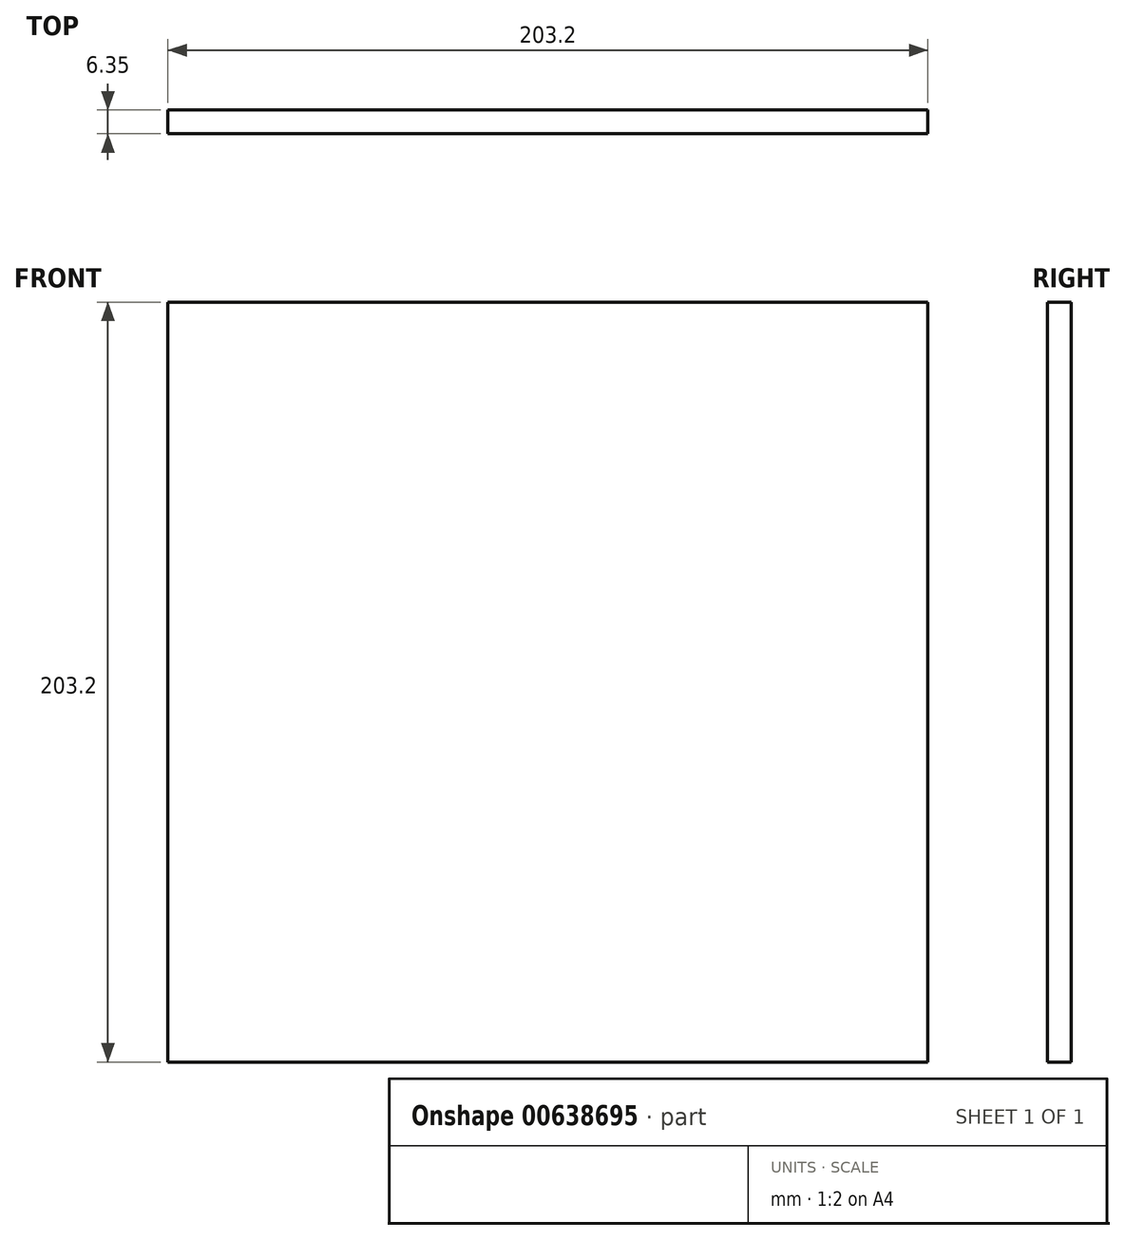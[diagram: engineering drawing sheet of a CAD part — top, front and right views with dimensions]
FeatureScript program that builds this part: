
annotation { "Feature Type Name" : "Feature", "Feature Type Description" : "" }
export const myFeature = defineFeature(function(context is Context, id is Id, definition is map)
    precondition{}
    {
        {
            var Q0;
            Q0=qCreatedBy(makeId("Front.planeOp"),FACE);
            var sketch = newSketch(context, id + "F0", { "sketchPlane" : qUnion([Q0])});
            skLineSegment(sketch, "E0.bottom", {"start": v(0, 0) * mm, "end": v(203.2, 0) * mm});
            skLineSegment(sketch, "E0.top", {"start": v(0, 203.2) * mm, "end": v(203.2, 203.2) * mm});
            skLineSegment(sketch, "E0.left", {"start": v(0, 0) * mm, "end": v(0, 203.2) * mm});
            skLineSegment(sketch, "E0.right", {"start": v(203.2, 0) * mm, "end": v(203.2, 203.2) * mm});
            skSolve(sketch);
        }
        {
            var Q0;
            Q0 = qSketchRegion(id + "F0", true);
            extrude(context, id + "F1", {"entities" : qUnion([Q0]), "depth" : 6.35 * mm, "offsetDistance" : 25.4 * mm});
        }
    });
